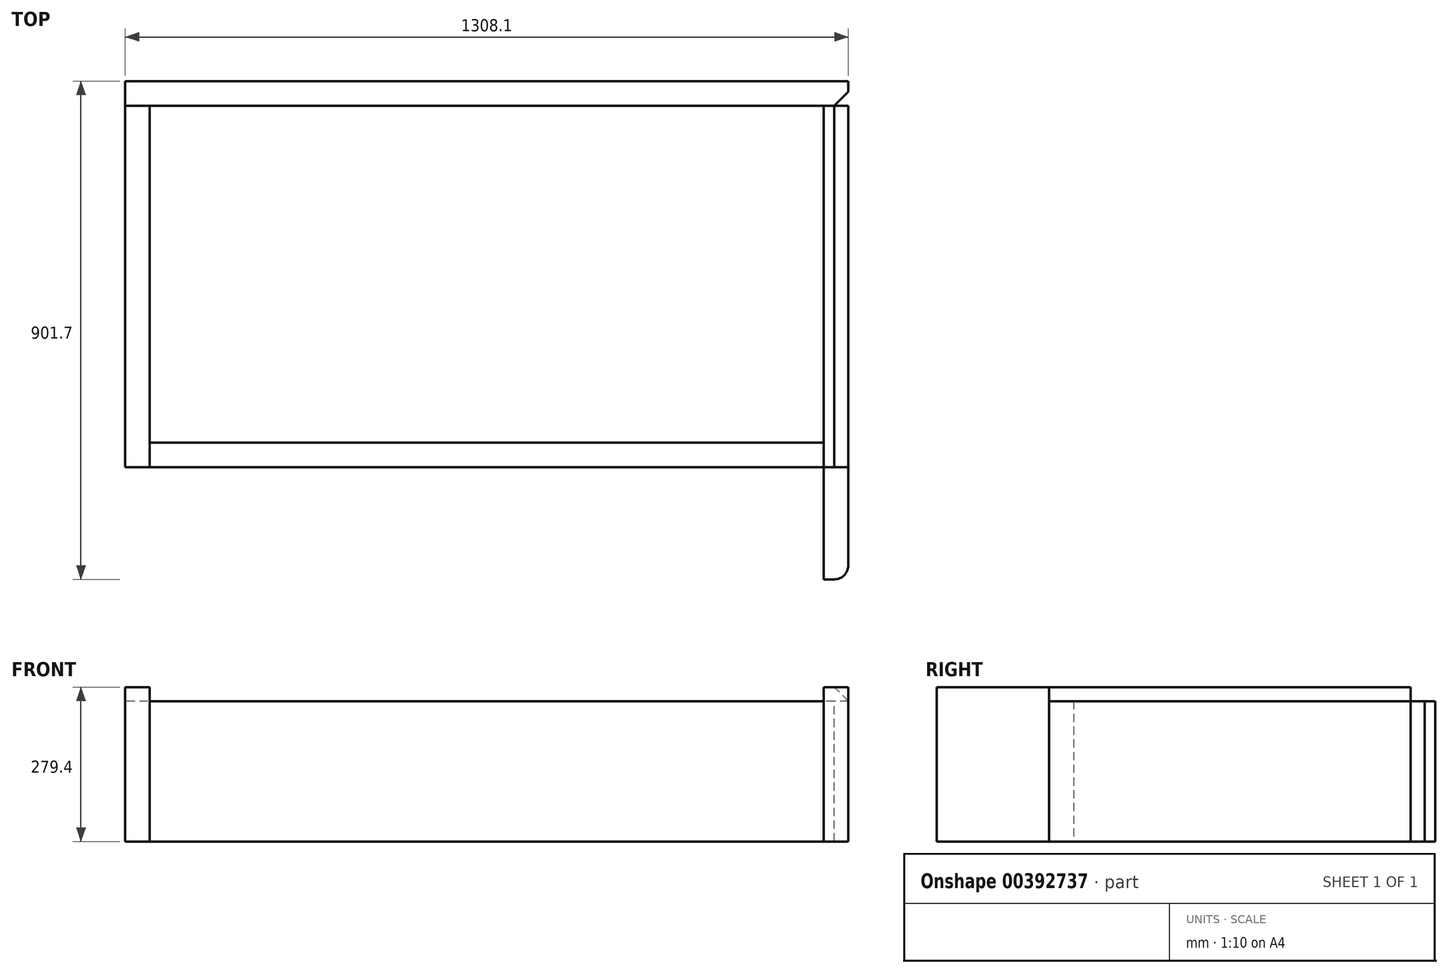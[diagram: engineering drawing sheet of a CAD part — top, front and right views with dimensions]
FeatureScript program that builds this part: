
annotation { "Feature Type Name" : "Feature", "Feature Type Description" : "" }
export const myFeature = defineFeature(function(context is Context, id is Id, definition is map)
    precondition{}
    {
        {
            var Q0;
            Q0=qCreatedBy(makeId("Top.planeOp"),FACE);
            var sketch = newSketch(context, id + "F0", { "sketchPlane" : qUnion([Q0])});
            skLineSegment(sketch, "E0.bottom", {"start": v(609.6, 304.8) * mm, "end": v(-609.6, 304.8) * mm});
            skLineSegment(sketch, "E0.top", {"start": v(609.6, -304.8) * mm, "end": v(-609.6, -304.8) * mm});
            skLineSegment(sketch, "E0.left", {"start": v(609.6, 304.8) * mm, "end": v(609.6, -304.8) * mm});
            skLineSegment(sketch, "E0.right", {"start": v(-609.6, 304.8) * mm, "end": v(-609.6, -304.8) * mm});
            skPoint(sketch, "E0.middle", {"position": v(0, 0) * mm});
            skLineSegment(sketch, "E1.0", {"start": v(-654.05, 349.25) * mm, "end": v(-654.05, -349.25) * mm});
            skLineSegment(sketch, "E1.1", {"start": v(654.05, 349.25) * mm, "end": v(-654.05, 349.25) * mm});
            skLineSegment(sketch, "E1.2", {"start": v(654.05, 349.25) * mm, "end": v(654.05, -349.25) * mm});
            skLineSegment(sketch, "E1.3", {"start": v(654.05, -349.25) * mm, "end": v(-654.05, -349.25) * mm});
            skLineSegment(sketch, "E2", {"start": v(609.6, -304.8) * mm, "end": v(609.6, -349.25) * mm});
            skLineSegment(sketch, "E3", {"start": v(0, 0) * mm, "end": v(0, 304.8) * mm, "construction": true});
            skLineSegment(sketch, "E4", {"start": v(609.6, 304.8) * mm, "end": v(654.05, 304.8) * mm});
            skLineSegment(sketch, "E5.MirrorCS", {"start": v(-609.6, -304.8) * mm, "end": v(-609.6, -349.25) * mm});
            skLineSegment(sketch, "E6.MirrorCS", {"start": v(-609.6, 304.8) * mm, "end": v(-654.05, 304.8) * mm});
            skSolve(sketch);
        }
        {
            var Q0;
            Q0=makeQuery(id+"F0.imprint","IMPRINT",FACE,{"disambiguationData":[TD([[makeQuery(id+"F0.imprint","IMPRINT",EDGE,{"derivedFrom":sQuery(id+"F0.wireOp",EDGE,"E0.left")}),1.0]])]});
            var Q1;
            {var subQ4=sQuery(id+"F0.wireOp",EDGE,"E5.MirrorCS");Q1=makeQuery(id+"F0.imprint","IMPRINT",FACE,{"disambiguationData":[TD([[makeQuery(id+"F0.imprint","IMPRINT",EDGE,{"derivedFrom":subQ4}),-1.0]])]});}
            extrude(context, id + "F1", {"entities" : qUnion([Q0, Q1]), "depth" : 279.4 * mm});
        }
        {
            var Q0;
            Q0=makeQuery(id+"F0.imprint","IMPRINT",FACE,{"disambiguationData":[TD([[makeQuery(id+"F0.imprint","IMPRINT",EDGE,{"derivedFrom":sQuery(id+"F0.wireOp",EDGE,"E0.bottom")}),-1.0]])]});
            var Q1;
            Q1=makeQuery(id+"F0.imprint","IMPRINT",FACE,{"disambiguationData":[TD([[makeQuery(id+"F0.imprint","IMPRINT",EDGE,{"derivedFrom":sQuery(id+"F0.wireOp",EDGE,"E0.top")}),1.0]])]});
            extrude(context, id + "F2", {"entities" : qUnion([Q0, Q1]), "depth" : 254 * mm});
        }
        {
            var Q0;
            {var subQ0=sQuery(id+"F0.wireOp",EDGE,"E1.3");Q0=makeQuery(id+"F1.opExtrude","SWEPT_FACE",FACE,{"disambiguationData":[OSD([subQ0]),TDD([makeQuery(id+"F0.imprint","IMPRINT",EDGE,{"disambiguationData":[TD([[makeQuery(id+"F0.imprint","INTERSECT",VERTEX,{"derivedFrom":[sQuery(id+"F0.wireOp",EDGE,"E1.2"),subQ0]}),-1.0]])],"derivedFrom":subQ0})])]});}
            extrude(context, id + "F3", {"entities" : qUnion([Q0]), "depth" : 203.2 * mm});
        }
        {
            var Q0;
            Q0=makeQuery(id+"F3.opExtrude","CAP_EDGE",EDGE,{"disambiguationData":[OSD([sQuery(id+"F0.wireOp",EDGE,"E1.2"),sQuery(id+"F0.wireOp",EDGE,"E1.3")])],"isStart":false});
            fillet(context, id + "F4", {"entities" : qUnion([Q0]), "radius" : 25.4 * mm, "tangentPropagation" : true, "allowEdgeOverflow" : false});
        }
        {
            var Q0;
            Q0=makeQuery(id+"F1.opExtrude","CAP_EDGE",EDGE,{"disambiguationData":[OSD([sQuery(id+"F0.wireOp",EDGE,"E1.2")])],"isStart":false});
            var Q1;
            Q1=makeQuery(id+"F2.opExtrude","SWEPT_EDGE",EDGE,{"disambiguationData":[OSD([sQuery(id+"F0.wireOp",EDGE,"E1.2"),sQuery(id+"F0.wireOp",EDGE,"E4")])]});
            chamfer(context, id + "F5", {"entities" : qUnion([Q0, Q1]), "width" : 25.4 * mm, "tangentPropagation" : true});
        }
    });
